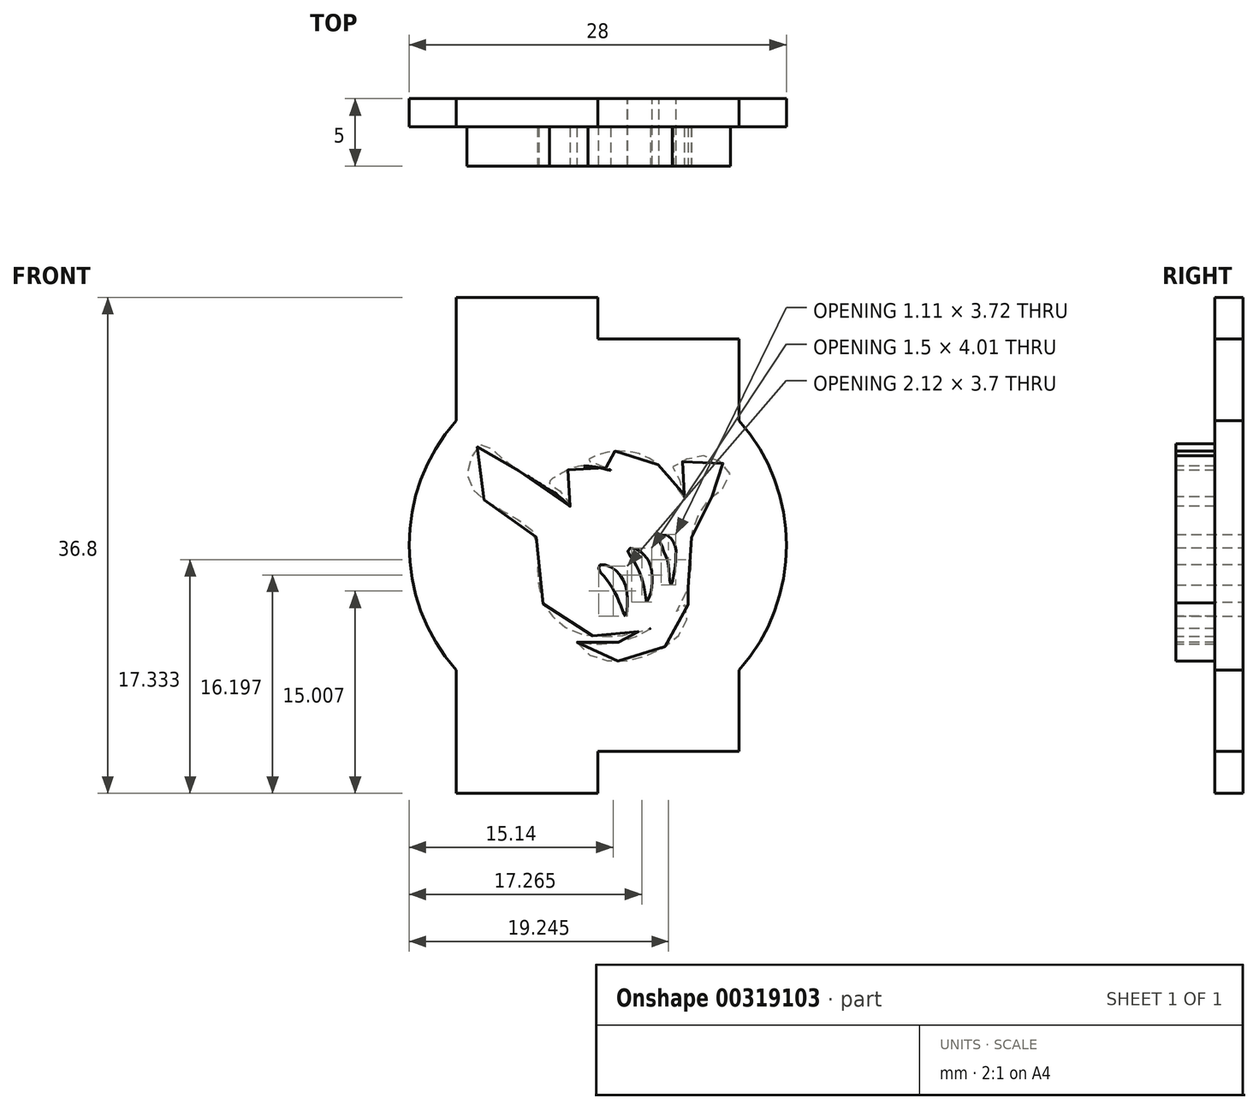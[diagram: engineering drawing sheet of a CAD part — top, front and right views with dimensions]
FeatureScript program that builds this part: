
annotation { "Feature Type Name" : "Feature", "Feature Type Description" : "" }
export const myFeature = defineFeature(function(context is Context, id is Id, definition is map)
    precondition{}
    {
        {
            var Q0;
            Q0=qCreatedBy(makeId("Front.planeOp"),FACE);
            var sketch = newSketch(context, id + "F0", { "sketchPlane" : qUnion([Q0])});
            skArc(sketch, "E0", {"start": v(-10.5, 9.26) * mm, "mid": v(-13.1, 4.95) * mm, "end": v(-14, 0) * mm});
            skLineSegment(sketch, "E1", {"start": v(0, 14) * mm, "end": v(0, 18.4) * mm});
            skLineSegment(sketch, "E2", {"start": v(0, 18.4) * mm, "end": v(-10.5, 18.4) * mm});
            skLineSegment(sketch, "E3", {"start": v(-10.5, 18.4) * mm, "end": v(-10.5, 9.26) * mm});
            skLineSegment(sketch, "E4", {"start": v(0, 14) * mm, "end": v(0, 15.3) * mm});
            skLineSegment(sketch, "E5", {"start": v(0, 15.3) * mm, "end": v(10.5, 15.3) * mm});
            skLineSegment(sketch, "E6", {"start": v(10.5, 15.3) * mm, "end": v(10.5, 9.26) * mm});
            skLineSegment(sketch, "E7", {"start": v(-17.75, 0) * mm, "end": v(17.38, 0) * mm, "construction": true});
            skArc(sketch, "E8.trimOffspring", {"start": v(14, 0) * mm, "mid": v(13.1, 4.95) * mm, "end": v(10.5, 9.26) * mm});
            skArc(sketch, "E9.MirrorCS", {"start": v(-10.5, -9.26) * mm, "mid": v(-13.1, -4.95) * mm, "end": v(-14, 0) * mm});
            skLineSegment(sketch, "E10.MirrorCS", {"start": v(-10.5, -18.4) * mm, "end": v(-10.5, -9.26) * mm});
            skLineSegment(sketch, "E11.MirrorCS", {"start": v(0, -18.4) * mm, "end": v(-10.5, -18.4) * mm});
            skLineSegment(sketch, "E12.MirrorCS", {"start": v(0, -14) * mm, "end": v(0, -18.4) * mm});
            skLineSegment(sketch, "E13.MirrorCS", {"start": v(0, -15.3) * mm, "end": v(10.5, -15.3) * mm});
            skLineSegment(sketch, "E14.MirrorCS", {"start": v(10.5, -15.3) * mm, "end": v(10.5, -9.26) * mm});
            skArc(sketch, "E15.MirrorCS", {"start": v(14, 0) * mm, "mid": v(13.1, -4.95) * mm, "end": v(10.5, -9.26) * mm});
            skFitSpline(sketch, "E16", {"points": [v(-1.55, -7.2) * mm, v(-1.16, -7.69) * mm, v(-0.74, -8.05) * mm, v(-0.21, -8.33) * mm, v(0.34, -8.51) * mm, v(1, -8.56) * mm, v(1.7, -8.58) * mm, v(2.39, -8.54) * mm, v(3.05, -8.38) * mm, v(3.7, -8.17) * mm, v(4.3, -7.9) * mm, v(4.9, -7.6) * mm, v(5.42, -7.2) * mm, v(5.89, -6.83) * mm, v(6.23, -6.33) * mm, v(6.55, -5.8) * mm, v(6.64, -5.18) * mm, v(6.67, -4.28) * mm, v(6.35, -4.63) * mm, v(5.63, -5.25) * mm, v(6.02, -4.65) * mm, v(6.41, -3.91) * mm, v(6.74, -3.04) * mm, v(6.87, -2.14) * mm, v(6.94, -1.31) * mm, v(6.94, -0.55) * mm, v(6.96, -0.1) * mm, v(6.97, 0.4) * mm, v(7, 0.89) * mm, v(7.12, 1.44) * mm, v(7.34, 2) * mm, v(7.63, 2.53) * mm, v(7.95, 3.02) * mm, v(8.37, 3.52) * mm, v(8.84, 3.9) * mm, v(9.24, 4.2) * mm, v(9.63, 4.53) * mm, v(9.83, 5.03) * mm, v(9.75, 5.55) * mm, v(9.42, 5.95) * mm, v(9.12, 6.21) * mm, v(8.65, 6.45) * mm, v(8.14, 6.61) * mm, v(7.65, 6.64) * mm, v(7.12, 6.54) * mm, v(6.64, 6.4) * mm, v(6.2, 6.17) * mm, v(5.85, 5.98) * mm, v(5.54, 5.76) * mm, v(5.76, 5.43) * mm, v(5.98, 5.04) * mm, v(6.14, 4.65) * mm, v(6.29, 4.24) * mm, v(6.4, 3.6) * mm, v(6.04, 4.06) * mm, v(5.78, 4.52) * mm, v(5.43, 4.97) * mm, v(5.12, 5.33) * mm, v(4.75, 5.72) * mm, v(4.41, 6.04) * mm, v(3.96, 6.37) * mm, v(3.5, 6.61) * mm, v(2.97, 6.82) * mm, v(2.33, 6.95) * mm, v(1.64, 7) * mm, v(1.01, 6.97) * mm, v(0.3, 6.8) * mm, v(-0.25, 6.6) * mm, v(-0.72, 6.3) * mm, v(-0.3, 6.1) * mm, v(0.17, 5.94) * mm, v(0.97, 5.57) * mm, v(0.35, 5.7) * mm, v(-0.37, 5.83) * mm, v(-0.98, 5.9) * mm, v(-1.6, 5.81) * mm, v(-2.25, 5.58) * mm, v(-2.8, 5.26) * mm, v(-3.59, 4.69) * mm, v(-3.04, 4.18) * mm, v(-2.48, 3.65) * mm, v(-2.05, 2.9) * mm, v(-2.78, 3.58) * mm, v(-3.8, 4.25) * mm, v(-4.78, 4.87) * mm, v(-5.68, 5.42) * mm, v(-6.37, 5.86) * mm, v(-6.98, 6.35) * mm, v(-7.49, 6.86) * mm, v(-8.01, 7.28) * mm, v(-8.64, 7.54) * mm, v(-9.18, 6.93) * mm, v(-9.56, 6.09) * mm, v(-9.67, 4.92) * mm, v(-9.23, 4.08) * mm, v(-8.43, 3.38) * mm, v(-7.4, 2.76) * mm, v(-6.46, 2.22) * mm, v(-5.5, 1.63) * mm, v(-4.7, 0.86) * mm, v(-4.37, -0.52) * mm, v(-4.48, -1.8) * mm, v(-4.37, -2.97) * mm, v(-4.15, -4.1) * mm, v(-3.72, -4.87) * mm, v(-3.02, -5.6) * mm, v(-2.18, -6.22) * mm, v(-1.12, -6.62) * mm, v(-0.12, -6.73) * mm, v(0.44, -6.77) * mm, v(0.99, -6.76) * mm, v(1.5, -6.74) * mm, v(2.12, -6.63) * mm, v(2.68, -6.5) * mm, v(3.3, -6.32) * mm, v(3.9, -6.19) * mm, v(3.38, -6.49) * mm, v(2.85, -6.77) * mm, v(2.32, -6.95) * mm, v(1.77, -7.12) * mm, v(1.16, -7.26) * mm, v(0.58, -7.33) * mm, v(0.1, -7.35) * mm, v(-0.39, -7.34) * mm, v(-0.83, -7.3) * mm, v(-1.27, -7.25) * mm, v(-1.55, -7.2) * mm]});
            skFitSpline(sketch, "E17", {"points": [v(2.08, -5.24) * mm, v(2.19, -4.7) * mm, v(2.2, -4.03) * mm, v(2.14, -3.35) * mm, v(1.93, -2.65) * mm, v(1.59, -2.13) * mm, v(1.07, -1.67) * mm, v(0.51, -1.44) * mm, v(0.12, -1.48) * mm, v(0.08, -1.8) * mm, v(0.3, -2.12) * mm, v(0.55, -2.39) * mm, v(0.84, -2.78) * mm, v(1.06, -3.15) * mm, v(1.25, -3.46) * mm, v(1.46, -3.87) * mm, v(1.62, -4.24) * mm, v(1.82, -4.79) * mm, v(2.08, -5.24) * mm]});
            skFitSpline(sketch, "E18", {"points": [v(3.64, -4.2) * mm, v(3.82, -3.86) * mm, v(3.99, -3.33) * mm, v(4.04, -2.81) * mm, v(4.04, -2.34) * mm, v(3.99, -1.78) * mm, v(3.83, -1.28) * mm, v(3.47, -0.73) * mm, v(3.16, -0.45) * mm, v(2.62, -0.2) * mm, v(2.23, -0.35) * mm, v(2.42, -0.84) * mm, v(2.75, -1.28) * mm, v(3, -1.73) * mm, v(3.24, -2.35) * mm, v(3.38, -2.87) * mm, v(3.47, -3.36) * mm, v(3.57, -3.8) * mm, v(3.64, -4.2) * mm]});
            skFitSpline(sketch, "E19", {"points": [v(5.42, -2.92) * mm, v(5.56, -2.59) * mm, v(5.66, -2.16) * mm, v(5.73, -1.69) * mm, v(5.8, -1.27) * mm, v(5.8, -0.78) * mm, v(5.81, -0.4) * mm, v(5.74, -0.08) * mm, v(5.62, 0.27) * mm, v(5.34, 0.63) * mm, v(4.99, 0.8) * mm, v(4.6, 0.66) * mm, v(4.6, 0.3) * mm, v(4.78, -0.14) * mm, v(4.92, -0.5) * mm, v(5.08, -0.91) * mm, v(5.2, -1.25) * mm, v(5.27, -1.63) * mm, v(5.3, -2.1) * mm, v(5.33, -2.53) * mm, v(5.42, -2.92) * mm]});
            skSolve(sketch);
        }
        {
            var Q0;
            Q0=makeQuery(id+"F0.imprint","IMPRINT",FACE,{"disambiguationData":[TD([[makeQuery(id+"F0.imprint","IMPRINT",EDGE,{"derivedFrom":sQuery(id+"F0.wireOp",EDGE,"E16")}),1.0]])]});
            extrude(context, id + "F1", {"entities" : qUnion([Q0]), "depth" : 5 * mm});
        }
        {
            var Q0;
            Q0=makeQuery(id+"F0.imprint","IMPRINT",FACE,{"disambiguationData":[TD([[makeQuery(id+"F0.imprint","IMPRINT",EDGE,{"derivedFrom":sQuery(id+"F0.wireOp",EDGE,"E0")}),1.0]])]});
            extrude(context, id + "F2", {"entities" : qUnion([Q0]), "operationType" : NewBodyOperationType.ADD, "depth" : 2.1 * mm});
        }
    });
